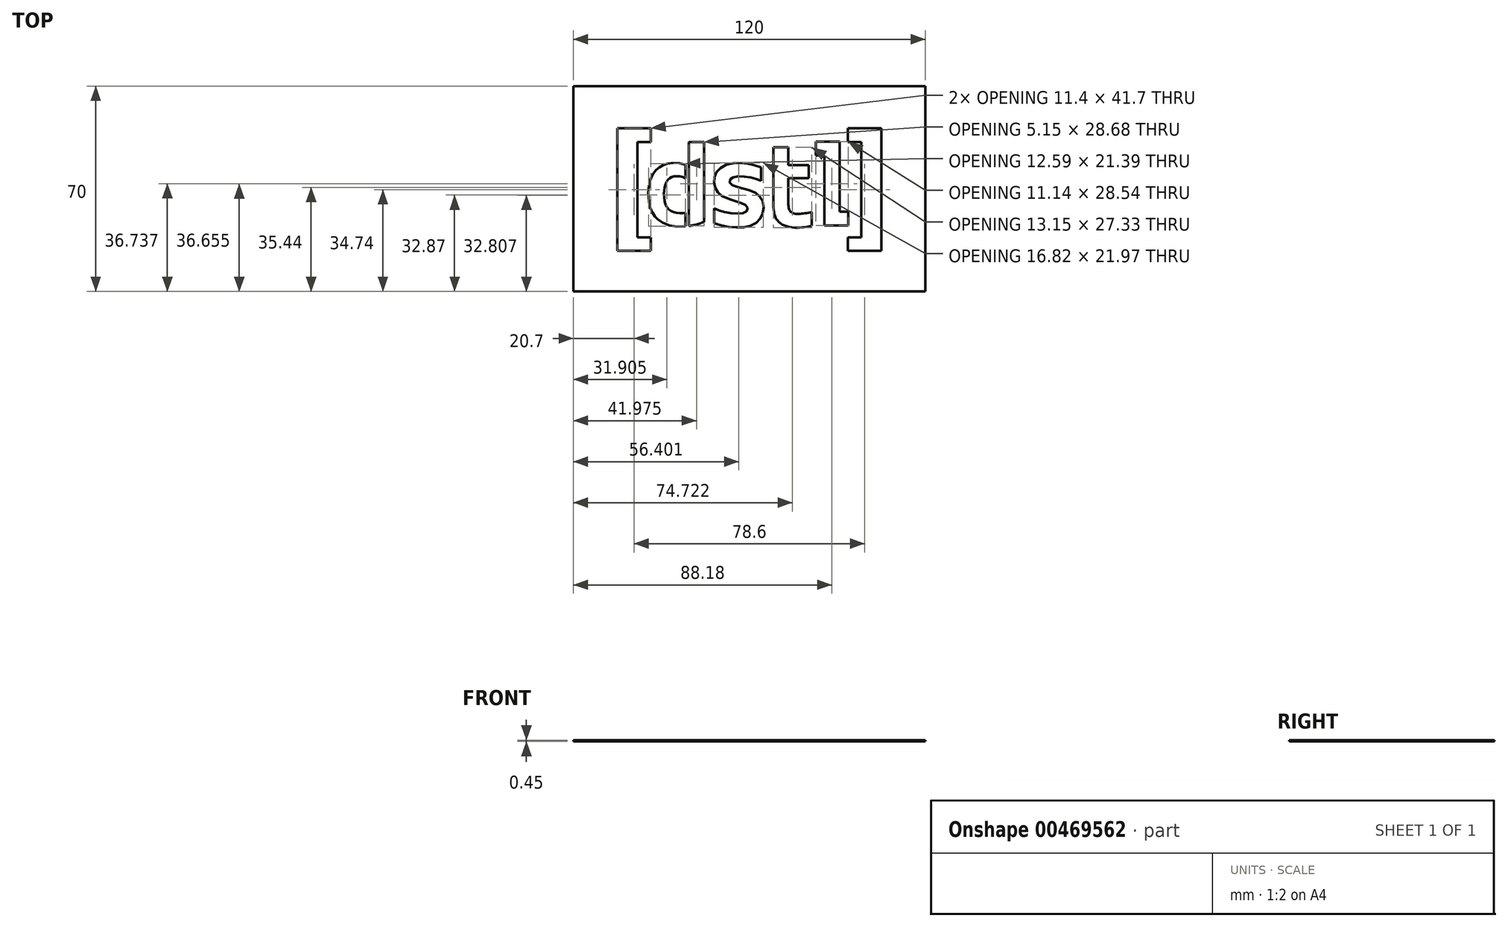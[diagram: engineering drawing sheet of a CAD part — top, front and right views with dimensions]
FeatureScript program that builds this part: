
annotation { "Feature Type Name" : "Feature", "Feature Type Description" : "" }
export const myFeature = defineFeature(function(context is Context, id is Id, definition is map)
    precondition{}
    {
        {
            var Q0;
            Q0=qCreatedBy(makeId("Top.planeOp"),FACE);
            var sketch = newSketch(context, id + "F0", { "sketchPlane" : qUnion([Q0])});
            skLineSegment(sketch, "E0", {"start": v(0, 0) * mm, "end": v(11.4, 0) * mm});
            skLineSegment(sketch, "E1", {"start": v(11.4, 0) * mm, "end": v(11.4, -4.6) * mm});
            skLineSegment(sketch, "E2", {"start": v(11.4, -4.6) * mm, "end": v(6.8, -4.6) * mm});
            skLineSegment(sketch, "E3", {"start": v(6.8, -4.6) * mm, "end": v(6.8, -37.1) * mm});
            skLineSegment(sketch, "E4", {"start": v(6.8, -37.1) * mm, "end": v(11.4, -37.1) * mm});
            skLineSegment(sketch, "E5", {"start": v(11.4, -37.1) * mm, "end": v(11.4, -41.7) * mm});
            skLineSegment(sketch, "E6", {"start": v(11.4, -41.7) * mm, "end": v(0, -41.7) * mm});
            skLineSegment(sketch, "E7", {"start": v(0, -41.7) * mm, "end": v(0, 0) * mm});
            skLineSegment(sketch, "E8", {"start": v(45, -41.81) * mm, "end": v(45, 0) * mm, "construction": true});
            skPoint(sketch, "E8.endSnap0", {"position": v(45, 0) * mm});
            skLineSegment(sketch, "E9.MirrorCS", {"start": v(90, 0) * mm, "end": v(78.6, 0) * mm});
            skLineSegment(sketch, "E10.MirrorCS", {"start": v(90, -41.7) * mm, "end": v(90, 0) * mm});
            skLineSegment(sketch, "E11.MirrorCS", {"start": v(78.6, 0) * mm, "end": v(78.6, -4.6) * mm});
            skLineSegment(sketch, "E12.MirrorCS", {"start": v(78.6, -4.6) * mm, "end": v(83.2, -4.6) * mm});
            skLineSegment(sketch, "E13.MirrorCS", {"start": v(83.2, -4.6) * mm, "end": v(83.2, -37.1) * mm});
            skLineSegment(sketch, "E14.MirrorCS", {"start": v(83.2, -37.1) * mm, "end": v(78.6, -37.1) * mm});
            skLineSegment(sketch, "E15.MirrorCS", {"start": v(78.6, -37.1) * mm, "end": v(78.6, -41.7) * mm});
            skLineSegment(sketch, "E16.MirrorCS", {"start": v(78.6, -41.7) * mm, "end": v(90, -41.7) * mm});
            skLineSegment(sketch, "E17", {"start": v(24.4, -4.6) * mm, "end": v(29.55, -4.6) * mm});
            skLineSegment(sketch, "E18", {"start": v(29.55, -4.6) * mm, "end": v(29.55, -31.86) * mm});
            skLineSegment(sketch, "E19", {"start": v(24.4, -4.6) * mm, "end": v(24.4, -12.95) * mm});
            skFitSpline(sketch, "E20", {"points": [v(24.4, -12.95) * mm, v(20.6, -11.81) * mm, v(17.04, -12.08) * mm, v(15.27, -12.7) * mm, v(13.52, -13.88) * mm, v(12.44, -15.12) * mm, v(11.7, -16.42) * mm, v(11.09, -18.19) * mm, v(10.77, -19.75) * mm, v(10.6, -21.69) * mm, v(10.62, -23.72) * mm, v(10.74, -24.98) * mm, v(10.94, -26.1) * mm, v(11.54, -27.95) * mm, v(12.68, -29.88) * mm, v(13.53, -30.84) * mm, v(17.26, -33) * mm, v(23.7, -33.36) * mm, v(27.7, -32.57) * mm, v(29.55, -31.86) * mm], "startDerivative": vector(-54.18, 26.92) * mm, "endDerivative": vector(34.88, 14.74) * mm});
            skLineSegment(sketch, "E21", {"start": v(24.4, -17.8) * mm, "end": v(24.4, -28.3) * mm});
            skFitSpline(sketch, "E22", {"points": [v(24.4, -17.8) * mm, v(21.8, -16.44) * mm, v(19.22, -16.38) * mm, v(17.7, -17.05) * mm, v(16.36, -19.04) * mm, v(15.9, -21.92) * mm, v(16.38, -25.76) * mm, v(17.9, -27.95) * mm, v(20.61, -28.87) * mm, v(23.28, -28.74) * mm, v(24.4, -28.3) * mm], "startDerivative": vector(-23.32, 15.43) * mm, "endDerivative": vector(14.35, 7.15) * mm});
            skLineSegment(sketch, "E23", {"start": v(49.02, -13.32) * mm, "end": v(49.02, -17.92) * mm});
            skFitSpline(sketch, "E24", {"points": [v(49.02, -13.32) * mm, v(45.84, -12.24) * mm, v(43.24, -11.85) * mm, v(39.54, -11.82) * mm, v(36.58, -12.65) * mm, v(34.47, -14.13) * mm, v(33.4, -15.66) * mm, v(33, -17.4) * mm, v(33.1, -19.25) * mm, v(33.62, -20.82) * mm, v(34.73, -22.29) * mm, v(37.02, -23.67) * mm, v(43.34, -25.87) * mm, v(43.68, -26.04) * mm, v(44.28, -26.68) * mm, v(44.37, -27.7) * mm, v(44.1, -28.23) * mm, v(43.22, -28.75) * mm, v(41.6, -29) * mm, v(39.2, -28.97) * mm, v(36.72, -28.58) * mm, v(34.87, -28.01) * mm, v(33.05, -27.27) * mm], "startDerivative": vector(-56.18, 21.1) * mm, "endDerivative": vector(-44.06, 24.4) * mm});
            skLineSegment(sketch, "E25", {"start": v(0, -22.6) * mm, "end": v(90, -22.6) * mm, "construction": true});
            skLineSegment(sketch, "E26", {"start": v(49.02, -17.92) * mm, "end": v(49.02, -22.6) * mm, "construction": true});
            skLineSegment(sketch, "E27", {"start": v(33.05, -27.27) * mm, "end": v(33.05, -22.6) * mm, "construction": true});
            skLineSegment(sketch, "E28", {"start": v(41.04, 0) * mm, "end": v(41.04, -41.81) * mm, "construction": true});
            skLineSegment(sketch, "E29", {"start": v(33.05, -27.27) * mm, "end": v(41.04, -27.27) * mm, "construction": true});
            skLineSegment(sketch, "E30", {"start": v(49.02, -17.92) * mm, "end": v(41.04, -17.92) * mm, "construction": true});
            skLineSegment(sketch, "E31.MirrorCS", {"start": v(33.05, -32.37) * mm, "end": v(33.05, -27.27) * mm});
            skFitSpline(sketch, "E32.MirrorCS", {"points": [v(33.05, -32.37) * mm, v(36.32, -33.29) * mm, v(39.54, -33.74) * mm, v(43.13, -33.67) * mm, v(45.85, -33) * mm, v(48.18, -31.49) * mm, v(49.18, -29.97) * mm, v(49.76, -28.27) * mm, v(49.66, -25.46) * mm, v(48.9, -23.6) * mm, v(47.58, -22.3) * mm, v(45.26, -21.2) * mm, v(40.04, -19.68) * mm, v(38.78, -19.06) * mm, v(38.3, -18.39) * mm, v(38.34, -17.67) * mm, v(38.63, -17.2) * mm, v(39.27, -16.76) * mm, v(40.67, -16.4) * mm, v(43.06, -16.38) * mm, v(45.33, -16.73) * mm, v(47.07, -17.2) * mm, v(49.02, -17.92) * mm], "startDerivative": vector(56.18, -21.1) * mm, "endDerivative": vector(44.25, -24.07) * mm});
            skLineSegment(sketch, "E33", {"start": v(53.15, -6.48) * mm, "end": v(58.3, -6.48) * mm});
            skLineSegment(sketch, "E34", {"start": v(58.3, -6.48) * mm, "end": v(58.3, -12.47) * mm});
            skLineSegment(sketch, "E35", {"start": v(58.3, -12.47) * mm, "end": v(65.22, -12.47) * mm});
            skLineSegment(sketch, "E36", {"start": v(65.22, -12.47) * mm, "end": v(65.22, -16.99) * mm});
            skLineSegment(sketch, "E37", {"start": v(65.22, -16.99) * mm, "end": v(58.3, -16.99) * mm});
            skLineSegment(sketch, "E38", {"start": v(58.3, -16.99) * mm, "end": v(58.3, -25.72) * mm});
            skLineSegment(sketch, "E39", {"start": v(53.15, -6.48) * mm, "end": v(53.15, -26.18) * mm});
            skLineSegment(sketch, "E40", {"start": v(66.3, -28.54) * mm, "end": v(66.3, -33.17) * mm});
            skFitSpline(sketch, "E41", {"points": [v(58.3, -25.72) * mm, v(58.52, -27.4) * mm, v(59.41, -28.66) * mm, v(61.86, -29.15) * mm, v(66.3, -28.54) * mm], "startDerivative": vector(0.36, -8.29) * mm, "endDerivative": vector(13.75, 2.6) * mm});
            skFitSpline(sketch, "E42", {"points": [v(53.15, -26.18) * mm, v(53.74, -29.93) * mm, v(55.7, -32.45) * mm, v(59.62, -33.74) * mm, v(63.8, -33.68) * mm, v(66.3, -33.17) * mm], "startDerivative": vector(1.32, -19.05) * mm, "endDerivative": vector(13.7, 3.36) * mm});
            skLineSegment(sketch, "E43", {"start": v(67.6, -4.58) * mm, "end": v(75.77, -4.58) * mm});
            skLineSegment(sketch, "E44", {"start": v(75.77, -4.58) * mm, "end": v(75.77, -28.44) * mm});
            skLineSegment(sketch, "E45", {"start": v(75.77, -28.44) * mm, "end": v(78.75, -28.44) * mm});
            skLineSegment(sketch, "E46", {"start": v(78.75, -28.44) * mm, "end": v(78.75, -33.12) * mm});
            skLineSegment(sketch, "E47", {"start": v(78.75, -33.12) * mm, "end": v(70.59, -33.12) * mm});
            skLineSegment(sketch, "E48", {"start": v(70.59, -33.12) * mm, "end": v(70.59, -9.27) * mm});
            skLineSegment(sketch, "E49", {"start": v(70.59, -9.27) * mm, "end": v(67.6, -9.27) * mm});
            skLineSegment(sketch, "E50", {"start": v(67.6, -9.27) * mm, "end": v(67.6, -4.58) * mm});
            skLineSegment(sketch, "E51.bottom", {"start": v(105, 14.4) * mm, "end": v(-15, 14.4) * mm});
            skLineSegment(sketch, "E51.top", {"start": v(105, -55.6) * mm, "end": v(-15, -55.6) * mm});
            skLineSegment(sketch, "E51.left", {"start": v(105, 14.4) * mm, "end": v(105, -55.6) * mm});
            skLineSegment(sketch, "E51.right", {"start": v(-15, 14.4) * mm, "end": v(-15, -55.6) * mm});
            skPoint(sketch, "E51.middle", {"position": v(45, -20.6) * mm});
            skLineSegment(sketch, "E52", {"start": v(24.4, -12.95) * mm, "end": v(24.4, -17.8) * mm});
            skLineSegment(sketch, "E53", {"start": v(23.2, -12.42) * mm, "end": v(23.2, -17.05) * mm});
            skLineSegment(sketch, "E54", {"start": v(24.4, -28.3) * mm, "end": v(24.4, -33.27) * mm});
            skLineSegment(sketch, "E55", {"start": v(23.2, -28.76) * mm, "end": v(23.2, -33.42) * mm});
            skSolve(sketch);
        }
        {
            var Q0;
            Q0=makeQuery(id+"F0.imprint","IMPRINT",FACE,{"disambiguationData":[TD([[makeQuery(id+"F0.imprint","IMPRINT",EDGE,{"derivedFrom":sQuery(id+"F0.wireOp",EDGE,"E0")}),1.0]])]});
            var Q1;
            {var subQ0=sQuery(id+"F0.wireOp",EDGE,"E52");Q1=makeQuery(id+"F0.imprint","IMPRINT",FACE,{"disambiguationData":[TD([[makeQuery(id+"F0.imprint","IMPRINT",EDGE,{"derivedFrom":subQ0}),-1.0]])]});}
            var Q2;
            {var subQ0=sQuery(id+"F0.wireOp",EDGE,"E21");Q2=makeQuery(id+"F0.imprint","IMPRINT",FACE,{"disambiguationData":[TD([[makeQuery(id+"F0.imprint","IMPRINT",EDGE,{"derivedFrom":subQ0}),-1.0]])]});}
            var Q3;
            {var subQ0=sQuery(id+"F0.wireOp",EDGE,"E54");Q3=makeQuery(id+"F0.imprint","IMPRINT",FACE,{"disambiguationData":[TD([[makeQuery(id+"F0.imprint","IMPRINT",EDGE,{"derivedFrom":subQ0}),-1.0]])]});}
            extrude(context, id + "F1", {"entities" : qUnion([Q0, Q1, Q2, Q3]), "depth" : 0.45 * mm});
        }
    });
